# Revit family: Doors_Industrial_BMP-Europe_DYNAMICROLL-CB-125
name_source: partatom
category: Doors
revit_build: Autodesk Revit 2015 (Build: 20140606_1530(x64)
units: mm (PartAtom-declared; Revit-internal decimal feet)

## types (1)
- Doors_Industrial_BMP-Europe_DYNAMICROLL-CB-125
    Analytic Construction = <None>
    BIMobject category = Industrial
    BIMobject category code = doors-industrial
    BIMobject main category = Doors
    BIMobject main category code = doors
    Brand url = http://www.bmpdoors.com
    Control Panel (Left / Right) = Yes
    Design country = Italy
    Edition number = 1
    Function = Interior
    Height = 1800 mm  [stored 5.90551 ft]
    Height control = 2000 mm  [stored 6.56168 ft]
    Height_check = 1800 mm  [stored 5.90551 ft]
    IFC Classification = Door
    Manufacturer country = Italy
    Manufacturer name = BMP Europe
    Masterformat 2014 Code = 08 11 16
    Masterformat 2014 Description = Aluminum Doors and Frames
    Material = <By Category>
    Material main = Aluminium
    Motor_Height = 2250 mm
    NBS Reference Code = 25-30-20-20
    NBS Reference Description = Doorset Systems
    Nominal height = 0 mm  [stored 0 ft]
    Nominal width = 0 mm  [stored 0 ft]
    OmniClass Code = 23-17 11 45 17
    OmniClass Description = Rapid Opening Doors
    Opening Height control = 0 mm  [stored 0 ft]
    Panels = 2
    Product Guid = b0c51faa-fc49-43b4-85a6-88ee64d4d69a
    Product SKU = DYNAMICROLL-CB-125
    Product data url = https://bimobject.com
    Product family = Doors / Industrial
    Product group = Dynamicroll
    Product url = http://www.bmpeurope.eu
    QR code = http://bimobject.com
    Rough Height = 0 mm  [stored 0 ft]
    Rough Width = 0 mm  [stored 0 ft]
    Technical description = http://www.bmpeurope.eu
    Thickness = 0 mm  [stored 0 ft]
    Total Height = 2250 mm
    Tr_height = 250 mm  [stored 0.82021 ft]
    Tr_width = 420 mm
    UNSPSC Code = 30171503
    Uniclass 1.4 Code = JL20
    Uniclass 1.4 Description = Doors
    Uniclass 2.0 Code = SS-25-30-20-20
    Uniclass 2.0 Description = Doorset Systems
    Uniclass 2015 Code = Pr_30_59_24_04
    Uniclass 2015 Name = Automatic revolving doorsets
    Uniformat II Code = B2030
    Uniformat II Description = Exterior Doors
    Vis_check = Yes
    Void_Opening = 1460 mm  [stored 4.79003 ft]
    Void_Opening_2 = 1460 mm  [stored 4.79003 ft]
    Void_Width = 850 mm  [stored 2.78871 ft]
    Void_distance = 25 mm  [stored 0.082021 ft]
    Void_distance_gate = 25 mm  [stored 0.082021 ft]
    Wall = 1900 mm
    Wall Closure = By host
    Width = 1800 mm  [stored 5.90551 ft]
    Windows OFF = No
    Windows ON = Yes
    Windows ON/OFF = Yes
    _Height = 1800 mm  [stored 5.90551 ft]
    _Width = 1800 mm  [stored 5.90551 ft]
    __Height = 1800 mm  [stored 5.90551 ft]
    __Opening Height = 0 mm  [stored 0 ft]
    __Width = 1800 mm  [stored 5.90551 ft]
    panel_l = Yes
    panel_r = No

note: [stored X ft] marks values corroborated as IEEE doubles in the binary element streams (Revit-internal decimal feet)

## geometry (parser evidence)
native form markers: Sweep x140
no freeform markers — native parametric forms only
